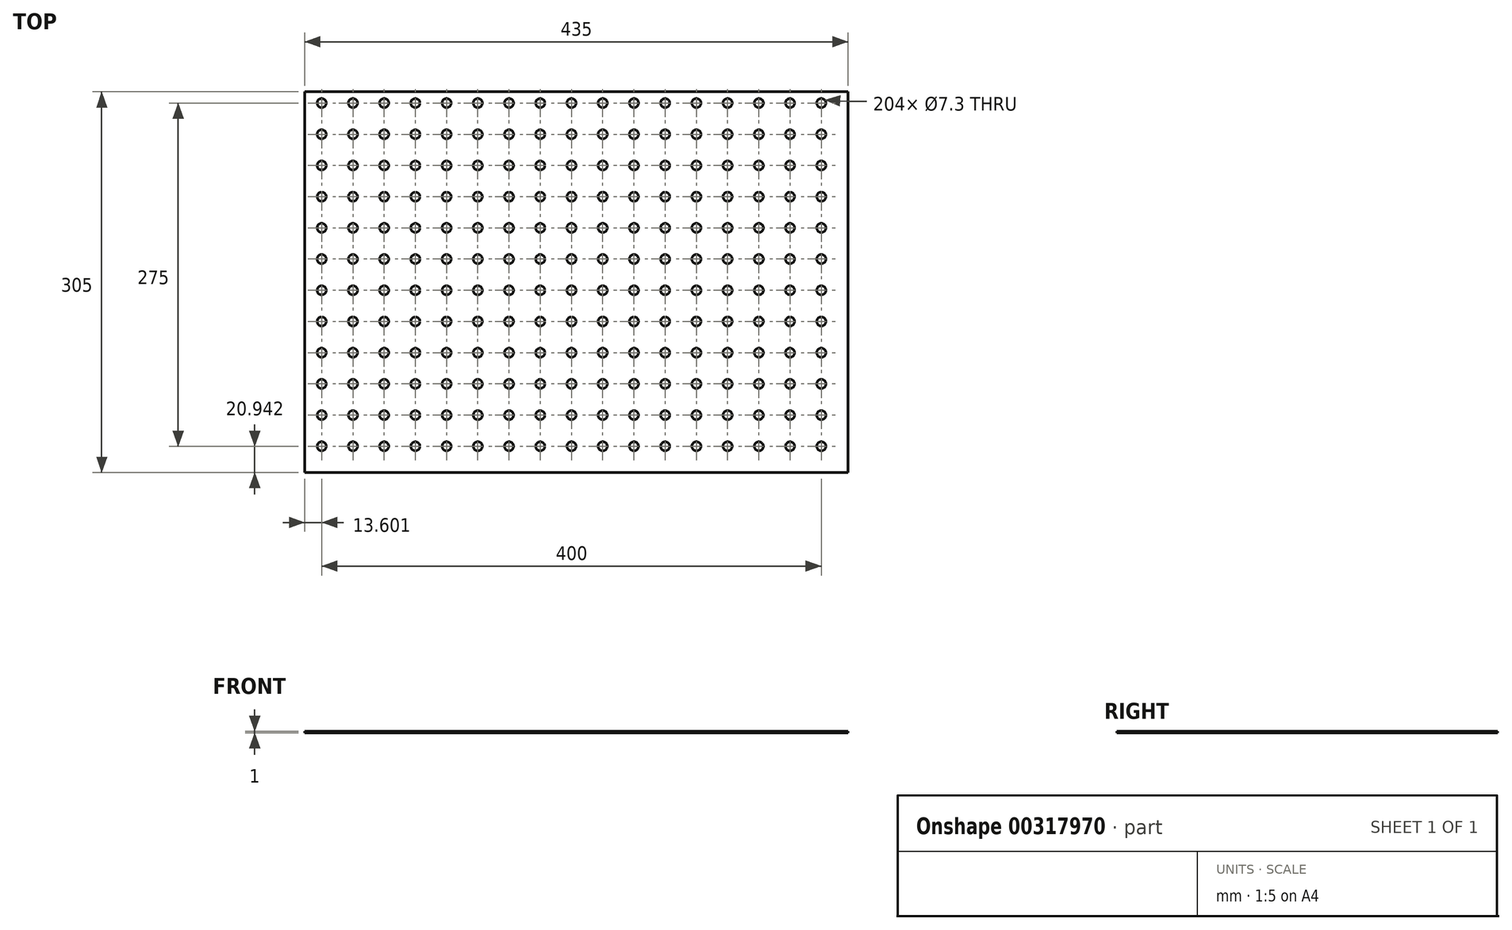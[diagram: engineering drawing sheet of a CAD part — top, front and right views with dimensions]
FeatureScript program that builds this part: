
annotation { "Feature Type Name" : "Feature", "Feature Type Description" : "" }
export const myFeature = defineFeature(function(context is Context, id is Id, definition is map)
    precondition{}
    {
        {
            var Q0;
            Q0=qCreatedBy(makeId("Top.planeOp"),FACE);
            var sketch = newSketch(context, id + "F0", { "sketchPlane" : qUnion([Q0])});
            skLineSegment(sketch, "E0.bottom", {"start": v(-215.73, 152.5) * mm, "end": v(219.27, 152.5) * mm});
            skLineSegment(sketch, "E0.top", {"start": v(-215.73, -152.5) * mm, "end": v(219.27, -152.5) * mm});
            skLineSegment(sketch, "E0.left", {"start": v(-215.73, 152.5) * mm, "end": v(-215.73, -152.5) * mm});
            skLineSegment(sketch, "E0.right", {"start": v(219.27, 152.5) * mm, "end": v(219.27, -152.5) * mm});
            skPoint(sketch, "E0.middle", {"position": v(1.77, 0) * mm});
            skSolve(sketch);
        }
        {
            var Q0;
            Q0 = qSketchRegion(id + "F0", true);
            extrude(context, id + "F1", {"entities" : qUnion([Q0]), "depth" : 1 * mm});
        }
        {
            var Q0;
            Q0=makeQuery(id+"F1.opExtrude","CAP_FACE",FACE,{"disambiguationData":[OSD([sQuery(id+"F0.wireOp",EDGE,"E0.bottom"),sQuery(id+"F0.wireOp",EDGE,"E0.top"),sQuery(id+"F0.wireOp",EDGE,"E0.left"),sQuery(id+"F0.wireOp",EDGE,"E0.right")])],"isStart":false});
            var sketch = newSketch(context, id + "F2", { "sketchPlane" : qUnion([Q0])});
            skLineSegment(sketch, "E1.bottom", {"start": v(-202.13, 143.44) * mm, "end": v(210.77, 143.44) * mm, "construction": true});
            skLineSegment(sketch, "E1.top", {"start": v(-202.13, -146.49) * mm, "end": v(210.77, -146.49) * mm, "construction": true});
            skLineSegment(sketch, "E1.left", {"start": v(-202.13, 143.44) * mm, "end": v(-202.13, -146.49) * mm, "construction": true});
            skLineSegment(sketch, "E1.right", {"start": v(210.77, 143.44) * mm, "end": v(210.77, -146.49) * mm, "construction": true});
            skPoint(sketch, "E1.middle", {"position": v(4.32, -1.52) * mm});
            skCircle(sketch, "E2", {"center": v(-202.13, 143.44) * mm, "radius": 3.65 * mm});
            skCircle(sketch, "E3.0.1.0", {"center": v(-202.13, 118.44) * mm, "radius": 3.65 * mm});
            skCircle(sketch, "E3.0.2.0", {"center": v(-202.13, 93.44) * mm, "radius": 3.65 * mm});
            skCircle(sketch, "E3.0.3.0", {"center": v(-202.13, 68.44) * mm, "radius": 3.65 * mm});
            skCircle(sketch, "E3.0.4.0", {"center": v(-202.13, 43.44) * mm, "radius": 3.65 * mm});
            skCircle(sketch, "E3.0.5.0", {"center": v(-202.13, 18.44) * mm, "radius": 3.65 * mm});
            skCircle(sketch, "E3.0.6.0", {"center": v(-202.13, -6.56) * mm, "radius": 3.65 * mm});
            skCircle(sketch, "E3.0.7.0", {"center": v(-202.13, -31.56) * mm, "radius": 3.65 * mm});
            skCircle(sketch, "E3.1.0.0", {"center": v(-177.13, 143.44) * mm, "radius": 3.65 * mm});
            skCircle(sketch, "E3.1.1.0", {"center": v(-177.13, 118.44) * mm, "radius": 3.65 * mm});
            skCircle(sketch, "E3.1.2.0", {"center": v(-177.13, 93.44) * mm, "radius": 3.65 * mm});
            skCircle(sketch, "E3.1.3.0", {"center": v(-177.13, 68.44) * mm, "radius": 3.65 * mm});
            skCircle(sketch, "E3.1.4.0", {"center": v(-177.13, 43.44) * mm, "radius": 3.65 * mm});
            skCircle(sketch, "E3.1.5.0", {"center": v(-177.13, 18.44) * mm, "radius": 3.65 * mm});
            skCircle(sketch, "E3.1.6.0", {"center": v(-177.13, -6.56) * mm, "radius": 3.65 * mm});
            skCircle(sketch, "E3.1.7.0", {"center": v(-177.13, -31.56) * mm, "radius": 3.65 * mm});
            skCircle(sketch, "E3.2.0.0", {"center": v(-152.13, 143.44) * mm, "radius": 3.65 * mm});
            skCircle(sketch, "E3.2.1.0", {"center": v(-152.13, 118.44) * mm, "radius": 3.65 * mm});
            skCircle(sketch, "E3.2.2.0", {"center": v(-152.13, 93.44) * mm, "radius": 3.65 * mm});
            skCircle(sketch, "E3.2.3.0", {"center": v(-152.13, 68.44) * mm, "radius": 3.65 * mm});
            skCircle(sketch, "E3.2.4.0", {"center": v(-152.13, 43.44) * mm, "radius": 3.65 * mm});
            skCircle(sketch, "E3.2.5.0", {"center": v(-152.13, 18.44) * mm, "radius": 3.65 * mm});
            skCircle(sketch, "E3.2.6.0", {"center": v(-152.13, -6.56) * mm, "radius": 3.65 * mm});
            skCircle(sketch, "E3.2.7.0", {"center": v(-152.13, -31.56) * mm, "radius": 3.65 * mm});
            skCircle(sketch, "E3.3.0.0", {"center": v(-127.13, 143.44) * mm, "radius": 3.65 * mm});
            skCircle(sketch, "E3.3.1.0", {"center": v(-127.13, 118.44) * mm, "radius": 3.65 * mm});
            skCircle(sketch, "E3.3.2.0", {"center": v(-127.13, 93.44) * mm, "radius": 3.65 * mm});
            skCircle(sketch, "E3.3.3.0", {"center": v(-127.13, 68.44) * mm, "radius": 3.65 * mm});
            skCircle(sketch, "E3.3.4.0", {"center": v(-127.13, 43.44) * mm, "radius": 3.65 * mm});
            skCircle(sketch, "E3.3.5.0", {"center": v(-127.13, 18.44) * mm, "radius": 3.65 * mm});
            skCircle(sketch, "E3.3.6.0", {"center": v(-127.13, -6.56) * mm, "radius": 3.65 * mm});
            skCircle(sketch, "E3.3.7.0", {"center": v(-127.13, -31.56) * mm, "radius": 3.65 * mm});
            skCircle(sketch, "E3.4.0.0", {"center": v(-102.13, 143.44) * mm, "radius": 3.65 * mm});
            skCircle(sketch, "E3.4.1.0", {"center": v(-102.13, 118.44) * mm, "radius": 3.65 * mm});
            skCircle(sketch, "E3.4.2.0", {"center": v(-102.13, 93.44) * mm, "radius": 3.65 * mm});
            skCircle(sketch, "E3.4.3.0", {"center": v(-102.13, 68.44) * mm, "radius": 3.65 * mm});
            skCircle(sketch, "E3.4.4.0", {"center": v(-102.13, 43.44) * mm, "radius": 3.65 * mm});
            skCircle(sketch, "E3.4.5.0", {"center": v(-102.13, 18.44) * mm, "radius": 3.65 * mm});
            skCircle(sketch, "E3.4.6.0", {"center": v(-102.13, -6.56) * mm, "radius": 3.65 * mm});
            skCircle(sketch, "E3.4.7.0", {"center": v(-102.13, -31.56) * mm, "radius": 3.65 * mm});
            skCircle(sketch, "E3.5.0.0", {"center": v(-77.13, 143.44) * mm, "radius": 3.65 * mm});
            skCircle(sketch, "E3.5.1.0", {"center": v(-77.13, 118.44) * mm, "radius": 3.65 * mm});
            skCircle(sketch, "E3.5.2.0", {"center": v(-77.13, 93.44) * mm, "radius": 3.65 * mm});
            skCircle(sketch, "E3.5.3.0", {"center": v(-77.13, 68.44) * mm, "radius": 3.65 * mm});
            skCircle(sketch, "E3.5.4.0", {"center": v(-77.13, 43.44) * mm, "radius": 3.65 * mm});
            skCircle(sketch, "E3.5.5.0", {"center": v(-77.13, 18.44) * mm, "radius": 3.65 * mm});
            skCircle(sketch, "E3.5.6.0", {"center": v(-77.13, -6.56) * mm, "radius": 3.65 * mm});
            skCircle(sketch, "E3.5.7.0", {"center": v(-77.13, -31.56) * mm, "radius": 3.65 * mm});
            skCircle(sketch, "E3.6.0.0", {"center": v(-52.13, 143.44) * mm, "radius": 3.65 * mm});
            skCircle(sketch, "E3.6.1.0", {"center": v(-52.13, 118.44) * mm, "radius": 3.65 * mm});
            skCircle(sketch, "E3.6.2.0", {"center": v(-52.13, 93.44) * mm, "radius": 3.65 * mm});
            skCircle(sketch, "E3.6.3.0", {"center": v(-52.13, 68.44) * mm, "radius": 3.65 * mm});
            skCircle(sketch, "E3.6.4.0", {"center": v(-52.13, 43.44) * mm, "radius": 3.65 * mm});
            skCircle(sketch, "E3.6.5.0", {"center": v(-52.13, 18.44) * mm, "radius": 3.65 * mm});
            skCircle(sketch, "E3.6.6.0", {"center": v(-52.13, -6.56) * mm, "radius": 3.65 * mm});
            skCircle(sketch, "E3.6.7.0", {"center": v(-52.13, -31.56) * mm, "radius": 3.65 * mm});
            skCircle(sketch, "E3.7.0.0", {"center": v(-27.13, 143.44) * mm, "radius": 3.65 * mm});
            skCircle(sketch, "E3.7.1.0", {"center": v(-27.13, 118.44) * mm, "radius": 3.65 * mm});
            skCircle(sketch, "E3.7.2.0", {"center": v(-27.13, 93.44) * mm, "radius": 3.65 * mm});
            skCircle(sketch, "E3.7.3.0", {"center": v(-27.13, 68.44) * mm, "radius": 3.65 * mm});
            skCircle(sketch, "E3.7.4.0", {"center": v(-27.13, 43.44) * mm, "radius": 3.65 * mm});
            skCircle(sketch, "E3.7.5.0", {"center": v(-27.13, 18.44) * mm, "radius": 3.65 * mm});
            skCircle(sketch, "E3.7.6.0", {"center": v(-27.13, -6.56) * mm, "radius": 3.65 * mm});
            skCircle(sketch, "E3.7.7.0", {"center": v(-27.13, -31.56) * mm, "radius": 3.65 * mm});
            skCircle(sketch, "E3.8.0.0", {"center": v(-2.13, 143.44) * mm, "radius": 3.65 * mm});
            skCircle(sketch, "E3.8.1.0", {"center": v(-2.13, 118.44) * mm, "radius": 3.65 * mm});
            skCircle(sketch, "E3.8.2.0", {"center": v(-2.13, 93.44) * mm, "radius": 3.65 * mm});
            skCircle(sketch, "E3.8.3.0", {"center": v(-2.13, 68.44) * mm, "radius": 3.65 * mm});
            skCircle(sketch, "E3.8.4.0", {"center": v(-2.13, 43.44) * mm, "radius": 3.65 * mm});
            skCircle(sketch, "E3.8.5.0", {"center": v(-2.13, 18.44) * mm, "radius": 3.65 * mm});
            skCircle(sketch, "E3.8.6.0", {"center": v(-2.13, -6.56) * mm, "radius": 3.65 * mm});
            skCircle(sketch, "E3.8.7.0", {"center": v(-2.13, -31.56) * mm, "radius": 3.65 * mm});
            skCircle(sketch, "E3.9.0.0", {"center": v(22.87, 143.44) * mm, "radius": 3.65 * mm});
            skCircle(sketch, "E3.9.1.0", {"center": v(22.87, 118.44) * mm, "radius": 3.65 * mm});
            skCircle(sketch, "E3.9.2.0", {"center": v(22.87, 93.44) * mm, "radius": 3.65 * mm});
            skCircle(sketch, "E3.9.3.0", {"center": v(22.87, 68.44) * mm, "radius": 3.65 * mm});
            skCircle(sketch, "E3.9.4.0", {"center": v(22.87, 43.44) * mm, "radius": 3.65 * mm});
            skCircle(sketch, "E3.9.5.0", {"center": v(22.87, 18.44) * mm, "radius": 3.65 * mm});
            skCircle(sketch, "E3.9.6.0", {"center": v(22.87, -6.56) * mm, "radius": 3.65 * mm});
            skCircle(sketch, "E3.9.7.0", {"center": v(22.87, -31.56) * mm, "radius": 3.65 * mm});
            skCircle(sketch, "E3.10.0.0", {"center": v(47.87, 143.44) * mm, "radius": 3.65 * mm});
            skCircle(sketch, "E3.10.1.0", {"center": v(47.87, 118.44) * mm, "radius": 3.65 * mm});
            skCircle(sketch, "E3.10.2.0", {"center": v(47.87, 93.44) * mm, "radius": 3.65 * mm});
            skCircle(sketch, "E3.10.3.0", {"center": v(47.87, 68.44) * mm, "radius": 3.65 * mm});
            skCircle(sketch, "E3.10.4.0", {"center": v(47.87, 43.44) * mm, "radius": 3.65 * mm});
            skCircle(sketch, "E3.10.5.0", {"center": v(47.87, 18.44) * mm, "radius": 3.65 * mm});
            skCircle(sketch, "E3.10.6.0", {"center": v(47.87, -6.56) * mm, "radius": 3.65 * mm});
            skCircle(sketch, "E3.10.7.0", {"center": v(47.87, -31.56) * mm, "radius": 3.65 * mm});
            skCircle(sketch, "E3.11.0.0", {"center": v(72.87, 143.44) * mm, "radius": 3.65 * mm});
            skCircle(sketch, "E3.11.1.0", {"center": v(72.87, 118.44) * mm, "radius": 3.65 * mm});
            skCircle(sketch, "E3.11.2.0", {"center": v(72.87, 93.44) * mm, "radius": 3.65 * mm});
            skCircle(sketch, "E3.11.3.0", {"center": v(72.87, 68.44) * mm, "radius": 3.65 * mm});
            skCircle(sketch, "E3.11.4.0", {"center": v(72.87, 43.44) * mm, "radius": 3.65 * mm});
            skCircle(sketch, "E3.11.5.0", {"center": v(72.87, 18.44) * mm, "radius": 3.65 * mm});
            skCircle(sketch, "E3.11.6.0", {"center": v(72.87, -6.56) * mm, "radius": 3.65 * mm});
            skCircle(sketch, "E3.11.7.0", {"center": v(72.87, -31.56) * mm, "radius": 3.65 * mm});
            skLineSegment(sketch, "E3.direction1", {"start": v(-202.13, 143.44) * mm, "end": v(-177.13, 143.44) * mm, "construction": true});
            skLineSegment(sketch, "E3.direction2", {"start": v(-202.13, 143.44) * mm, "end": v(-202.13, 118.44) * mm, "construction": true});
            skCircle(sketch, "E4.0.12.0", {"center": v(97.87, 143.44) * mm, "radius": 3.65 * mm});
            skCircle(sketch, "E4.0.12.1", {"center": v(97.87, 118.44) * mm, "radius": 3.65 * mm});
            skCircle(sketch, "E4.0.12.2", {"center": v(97.87, 93.44) * mm, "radius": 3.65 * mm});
            skCircle(sketch, "E4.0.12.3", {"center": v(97.87, 68.44) * mm, "radius": 3.65 * mm});
            skCircle(sketch, "E4.0.12.4", {"center": v(97.87, 43.44) * mm, "radius": 3.65 * mm});
            skCircle(sketch, "E4.0.12.5", {"center": v(97.87, 18.44) * mm, "radius": 3.65 * mm});
            skCircle(sketch, "E4.0.12.6", {"center": v(97.87, -6.56) * mm, "radius": 3.65 * mm});
            skCircle(sketch, "E4.0.12.7", {"center": v(97.87, -31.56) * mm, "radius": 3.65 * mm});
            skCircle(sketch, "E4.0.13.0", {"center": v(122.87, 143.44) * mm, "radius": 3.65 * mm});
            skCircle(sketch, "E4.0.13.1", {"center": v(122.87, 118.44) * mm, "radius": 3.65 * mm});
            skCircle(sketch, "E4.0.13.2", {"center": v(122.87, 93.44) * mm, "radius": 3.65 * mm});
            skCircle(sketch, "E4.0.13.3", {"center": v(122.87, 68.44) * mm, "radius": 3.65 * mm});
            skCircle(sketch, "E4.0.13.4", {"center": v(122.87, 43.44) * mm, "radius": 3.65 * mm});
            skCircle(sketch, "E4.0.13.5", {"center": v(122.87, 18.44) * mm, "radius": 3.65 * mm});
            skCircle(sketch, "E4.0.13.6", {"center": v(122.87, -6.56) * mm, "radius": 3.65 * mm});
            skCircle(sketch, "E4.0.13.7", {"center": v(122.87, -31.56) * mm, "radius": 3.65 * mm});
            skCircle(sketch, "E4.0.14.0", {"center": v(147.87, 143.44) * mm, "radius": 3.65 * mm});
            skCircle(sketch, "E4.0.14.1", {"center": v(147.87, 118.44) * mm, "radius": 3.65 * mm});
            skCircle(sketch, "E4.0.14.2", {"center": v(147.87, 93.44) * mm, "radius": 3.65 * mm});
            skCircle(sketch, "E4.0.14.3", {"center": v(147.87, 68.44) * mm, "radius": 3.65 * mm});
            skCircle(sketch, "E4.0.14.4", {"center": v(147.87, 43.44) * mm, "radius": 3.65 * mm});
            skCircle(sketch, "E4.0.14.5", {"center": v(147.87, 18.44) * mm, "radius": 3.65 * mm});
            skCircle(sketch, "E4.0.14.6", {"center": v(147.87, -6.56) * mm, "radius": 3.65 * mm});
            skCircle(sketch, "E4.0.14.7", {"center": v(147.87, -31.56) * mm, "radius": 3.65 * mm});
            skCircle(sketch, "E4.0.15.0", {"center": v(172.87, 143.44) * mm, "radius": 3.65 * mm});
            skCircle(sketch, "E4.0.15.1", {"center": v(172.87, 118.44) * mm, "radius": 3.65 * mm});
            skCircle(sketch, "E4.0.15.2", {"center": v(172.87, 93.44) * mm, "radius": 3.65 * mm});
            skCircle(sketch, "E4.0.15.3", {"center": v(172.87, 68.44) * mm, "radius": 3.65 * mm});
            skCircle(sketch, "E4.0.15.4", {"center": v(172.87, 43.44) * mm, "radius": 3.65 * mm});
            skCircle(sketch, "E4.0.15.5", {"center": v(172.87, 18.44) * mm, "radius": 3.65 * mm});
            skCircle(sketch, "E4.0.15.6", {"center": v(172.87, -6.56) * mm, "radius": 3.65 * mm});
            skCircle(sketch, "E4.0.15.7", {"center": v(172.87, -31.56) * mm, "radius": 3.65 * mm});
            skCircle(sketch, "E4.0.16.0", {"center": v(197.87, 143.44) * mm, "radius": 3.65 * mm});
            skCircle(sketch, "E4.0.16.1", {"center": v(197.87, 118.44) * mm, "radius": 3.65 * mm});
            skCircle(sketch, "E4.0.16.2", {"center": v(197.87, 93.44) * mm, "radius": 3.65 * mm});
            skCircle(sketch, "E4.0.16.3", {"center": v(197.87, 68.44) * mm, "radius": 3.65 * mm});
            skCircle(sketch, "E4.0.16.4", {"center": v(197.87, 43.44) * mm, "radius": 3.65 * mm});
            skCircle(sketch, "E4.0.16.5", {"center": v(197.87, 18.44) * mm, "radius": 3.65 * mm});
            skCircle(sketch, "E4.0.16.6", {"center": v(197.87, -6.56) * mm, "radius": 3.65 * mm});
            skCircle(sketch, "E4.0.16.7", {"center": v(197.87, -31.56) * mm, "radius": 3.65 * mm});
            skCircle(sketch, "E5.0.0.8", {"center": v(-202.13, -56.56) * mm, "radius": 3.65 * mm});
            skCircle(sketch, "E5.0.0.9", {"center": v(-202.13, -81.56) * mm, "radius": 3.65 * mm});
            skCircle(sketch, "E5.0.0.10", {"center": v(-202.13, -106.56) * mm, "radius": 3.65 * mm});
            skCircle(sketch, "E5.0.0.11", {"center": v(-202.13, -131.56) * mm, "radius": 3.65 * mm});
            skCircle(sketch, "E5.0.1.8", {"center": v(-177.13, -56.56) * mm, "radius": 3.65 * mm});
            skCircle(sketch, "E5.0.1.9", {"center": v(-177.13, -81.56) * mm, "radius": 3.65 * mm});
            skCircle(sketch, "E5.0.1.10", {"center": v(-177.13, -106.56) * mm, "radius": 3.65 * mm});
            skCircle(sketch, "E5.0.1.11", {"center": v(-177.13, -131.56) * mm, "radius": 3.65 * mm});
            skCircle(sketch, "E5.0.2.8", {"center": v(-152.13, -56.56) * mm, "radius": 3.65 * mm});
            skCircle(sketch, "E5.0.2.9", {"center": v(-152.13, -81.56) * mm, "radius": 3.65 * mm});
            skCircle(sketch, "E5.0.2.10", {"center": v(-152.13, -106.56) * mm, "radius": 3.65 * mm});
            skCircle(sketch, "E5.0.2.11", {"center": v(-152.13, -131.56) * mm, "radius": 3.65 * mm});
            skCircle(sketch, "E5.0.3.8", {"center": v(-127.13, -56.56) * mm, "radius": 3.65 * mm});
            skCircle(sketch, "E5.0.3.9", {"center": v(-127.13, -81.56) * mm, "radius": 3.65 * mm});
            skCircle(sketch, "E5.0.3.10", {"center": v(-127.13, -106.56) * mm, "radius": 3.65 * mm});
            skCircle(sketch, "E5.0.3.11", {"center": v(-127.13, -131.56) * mm, "radius": 3.65 * mm});
            skCircle(sketch, "E5.0.4.8", {"center": v(-102.13, -56.56) * mm, "radius": 3.65 * mm});
            skCircle(sketch, "E5.0.4.9", {"center": v(-102.13, -81.56) * mm, "radius": 3.65 * mm});
            skCircle(sketch, "E5.0.4.10", {"center": v(-102.13, -106.56) * mm, "radius": 3.65 * mm});
            skCircle(sketch, "E5.0.4.11", {"center": v(-102.13, -131.56) * mm, "radius": 3.65 * mm});
            skCircle(sketch, "E5.0.5.8", {"center": v(-77.13, -56.56) * mm, "radius": 3.65 * mm});
            skCircle(sketch, "E5.0.5.9", {"center": v(-77.13, -81.56) * mm, "radius": 3.65 * mm});
            skCircle(sketch, "E5.0.5.10", {"center": v(-77.13, -106.56) * mm, "radius": 3.65 * mm});
            skCircle(sketch, "E5.0.5.11", {"center": v(-77.13, -131.56) * mm, "radius": 3.65 * mm});
            skCircle(sketch, "E5.0.6.8", {"center": v(-52.13, -56.56) * mm, "radius": 3.65 * mm});
            skCircle(sketch, "E5.0.6.9", {"center": v(-52.13, -81.56) * mm, "radius": 3.65 * mm});
            skCircle(sketch, "E5.0.6.10", {"center": v(-52.13, -106.56) * mm, "radius": 3.65 * mm});
            skCircle(sketch, "E5.0.6.11", {"center": v(-52.13, -131.56) * mm, "radius": 3.65 * mm});
            skCircle(sketch, "E5.0.7.8", {"center": v(-27.13, -56.56) * mm, "radius": 3.65 * mm});
            skCircle(sketch, "E5.0.7.9", {"center": v(-27.13, -81.56) * mm, "radius": 3.65 * mm});
            skCircle(sketch, "E5.0.7.10", {"center": v(-27.13, -106.56) * mm, "radius": 3.65 * mm});
            skCircle(sketch, "E5.0.7.11", {"center": v(-27.13, -131.56) * mm, "radius": 3.65 * mm});
            skCircle(sketch, "E5.0.8.8", {"center": v(-2.13, -56.56) * mm, "radius": 3.65 * mm});
            skCircle(sketch, "E5.0.8.9", {"center": v(-2.13, -81.56) * mm, "radius": 3.65 * mm});
            skCircle(sketch, "E5.0.8.10", {"center": v(-2.13, -106.56) * mm, "radius": 3.65 * mm});
            skCircle(sketch, "E5.0.8.11", {"center": v(-2.13, -131.56) * mm, "radius": 3.65 * mm});
            skCircle(sketch, "E5.0.9.8", {"center": v(22.87, -56.56) * mm, "radius": 3.65 * mm});
            skCircle(sketch, "E5.0.9.9", {"center": v(22.87, -81.56) * mm, "radius": 3.65 * mm});
            skCircle(sketch, "E5.0.9.10", {"center": v(22.87, -106.56) * mm, "radius": 3.65 * mm});
            skCircle(sketch, "E5.0.9.11", {"center": v(22.87, -131.56) * mm, "radius": 3.65 * mm});
            skCircle(sketch, "E5.0.10.8", {"center": v(47.87, -56.56) * mm, "radius": 3.65 * mm});
            skCircle(sketch, "E5.0.10.9", {"center": v(47.87, -81.56) * mm, "radius": 3.65 * mm});
            skCircle(sketch, "E5.0.10.10", {"center": v(47.87, -106.56) * mm, "radius": 3.65 * mm});
            skCircle(sketch, "E5.0.10.11", {"center": v(47.87, -131.56) * mm, "radius": 3.65 * mm});
            skCircle(sketch, "E5.0.11.8", {"center": v(72.87, -56.56) * mm, "radius": 3.65 * mm});
            skCircle(sketch, "E5.0.11.9", {"center": v(72.87, -81.56) * mm, "radius": 3.65 * mm});
            skCircle(sketch, "E5.0.11.10", {"center": v(72.87, -106.56) * mm, "radius": 3.65 * mm});
            skCircle(sketch, "E5.0.11.11", {"center": v(72.87, -131.56) * mm, "radius": 3.65 * mm});
            skCircle(sketch, "E5.0.12.8", {"center": v(97.87, -56.56) * mm, "radius": 3.65 * mm});
            skCircle(sketch, "E5.0.12.9", {"center": v(97.87, -81.56) * mm, "radius": 3.65 * mm});
            skCircle(sketch, "E5.0.12.10", {"center": v(97.87, -106.56) * mm, "radius": 3.65 * mm});
            skCircle(sketch, "E5.0.12.11", {"center": v(97.87, -131.56) * mm, "radius": 3.65 * mm});
            skCircle(sketch, "E5.0.13.8", {"center": v(122.87, -56.56) * mm, "radius": 3.65 * mm});
            skCircle(sketch, "E5.0.13.9", {"center": v(122.87, -81.56) * mm, "radius": 3.65 * mm});
            skCircle(sketch, "E5.0.13.10", {"center": v(122.87, -106.56) * mm, "radius": 3.65 * mm});
            skCircle(sketch, "E5.0.13.11", {"center": v(122.87, -131.56) * mm, "radius": 3.65 * mm});
            skCircle(sketch, "E5.0.14.8", {"center": v(147.87, -56.56) * mm, "radius": 3.65 * mm});
            skCircle(sketch, "E5.0.14.9", {"center": v(147.87, -81.56) * mm, "radius": 3.65 * mm});
            skCircle(sketch, "E5.0.14.10", {"center": v(147.87, -106.56) * mm, "radius": 3.65 * mm});
            skCircle(sketch, "E5.0.14.11", {"center": v(147.87, -131.56) * mm, "radius": 3.65 * mm});
            skCircle(sketch, "E5.0.15.8", {"center": v(172.87, -56.56) * mm, "radius": 3.65 * mm});
            skCircle(sketch, "E5.0.15.9", {"center": v(172.87, -81.56) * mm, "radius": 3.65 * mm});
            skCircle(sketch, "E5.0.15.10", {"center": v(172.87, -106.56) * mm, "radius": 3.65 * mm});
            skCircle(sketch, "E5.0.15.11", {"center": v(172.87, -131.56) * mm, "radius": 3.65 * mm});
            skCircle(sketch, "E5.0.16.8", {"center": v(197.87, -56.56) * mm, "radius": 3.65 * mm});
            skCircle(sketch, "E5.0.16.9", {"center": v(197.87, -81.56) * mm, "radius": 3.65 * mm});
            skCircle(sketch, "E5.0.16.10", {"center": v(197.87, -106.56) * mm, "radius": 3.65 * mm});
            skCircle(sketch, "E5.0.16.11", {"center": v(197.87, -131.56) * mm, "radius": 3.65 * mm});
            skSolve(sketch);
        }
        {
            var Q0;
            Q0 = qSketchRegion(id + "F2", true);
            extrude(context, id + "F3", {"entities" : qUnion([Q0]), "operationType" : NewBodyOperationType.REMOVE, "oppositeDirection" : true, "depth" : 25.4 * mm});
        }
    });
